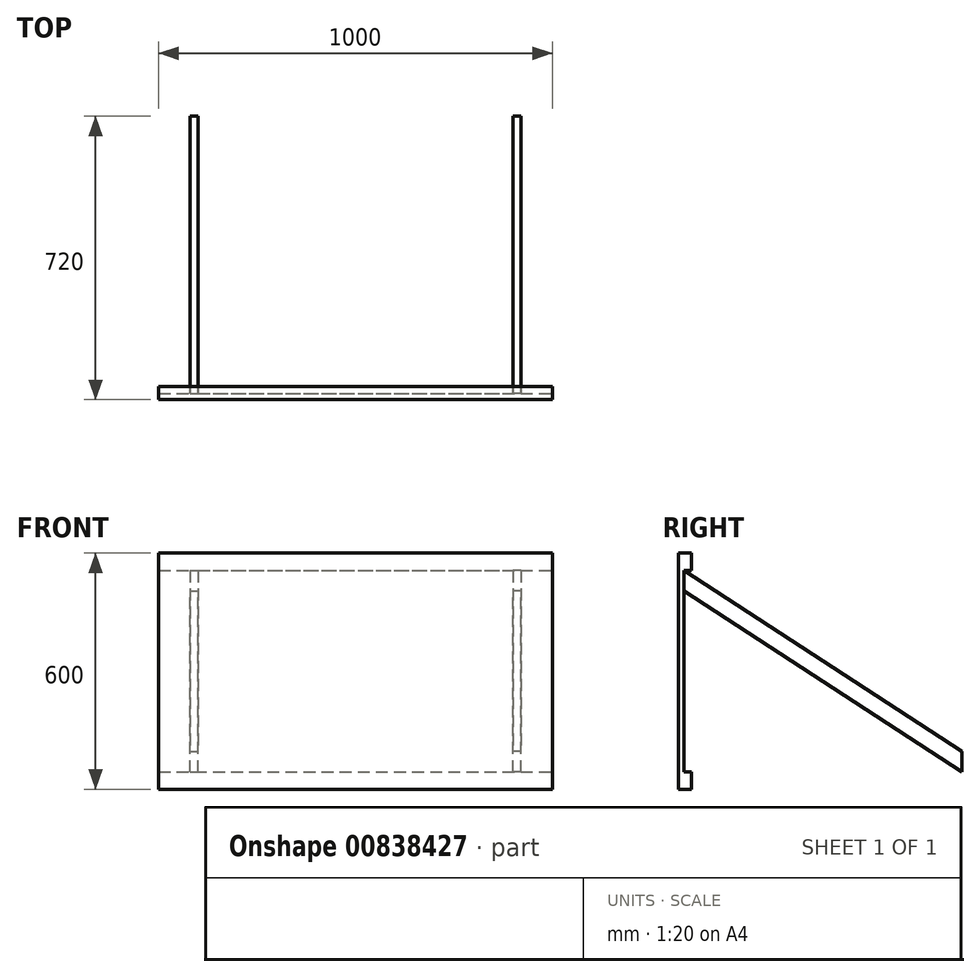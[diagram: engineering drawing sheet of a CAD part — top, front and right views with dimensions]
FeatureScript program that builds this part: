
annotation { "Feature Type Name" : "Feature", "Feature Type Description" : "" }
export const myFeature = defineFeature(function(context is Context, id is Id, definition is map)
    precondition{}
    {
        {
            var Q0;
            Q0=qCreatedBy(makeId("Front.planeOp"),FACE);
            var sketch = newSketch(context, id + "F0", { "sketchPlane" : qUnion([Q0])});
            skLineSegment(sketch, "E0.bottom", {"start": v(500, 0) * mm, "end": v(-500, 0) * mm});
            skLineSegment(sketch, "E0.top", {"start": v(500, 600) * mm, "end": v(-500, 600) * mm});
            skLineSegment(sketch, "E0.left", {"start": v(500, 0) * mm, "end": v(500, 600) * mm});
            skLineSegment(sketch, "E0.right", {"start": v(-500, 0) * mm, "end": v(-500, 600) * mm});
            skSolve(sketch);
        }
        {
            var Q0;
            Q0 = qSketchRegion(id + "F0", true);
            extrude(context, id + "F1", {"entities" : qUnion([Q0]), "depth" : 15 * mm, "offsetDistance" : 25 * mm});
        }
        {
            var Q0;
            Q0=makeQuery(id+"F1.opExtrude","CAP_FACE",FACE,{"disambiguationData":[OSD([sQuery(id+"F0.wireOp",EDGE,"E0.bottom"),sQuery(id+"F0.wireOp",EDGE,"E0.top"),sQuery(id+"F0.wireOp",EDGE,"E0.left"),sQuery(id+"F0.wireOp",EDGE,"E0.right")])],"isStart":true});
            cPlane(context, id + "F2", {"entities" : qUnion([Q0]), "cplaneType" : CPlaneType.OFFSET, "offset" : 0 * mm, "width" : 150 * mm, "height" : 150 * mm});
        }
        {
            var Q0;
            Q0=qCreatedBy(id+"F2.planeOp",FACE);
            var sketch = newSketch(context, id + "F3", { "sketchPlane" : qUnion([Q0])});
            skLineSegment(sketch, "E1.bottom", {"start": v(500, 0) * mm, "end": v(-500, 0) * mm});
            skLineSegment(sketch, "E1.top", {"start": v(500, 44) * mm, "end": v(-500, 44) * mm});
            skLineSegment(sketch, "E1.left", {"start": v(500, 0) * mm, "end": v(500, 44) * mm});
            skLineSegment(sketch, "E1.right", {"start": v(-500, 0) * mm, "end": v(-500, 44) * mm});
            skSolve(sketch);
        }
        {
            var Q0;
            Q0 = qSketchRegion(id + "F3", true);
            extrude(context, id + "F4", {"entities" : qUnion([Q0]), "operationType" : NewBodyOperationType.ADD, "depth" : 18 * mm, "offsetDistance" : 25 * mm});
        }
        {
            var Q0;
            Q0=qCreatedBy(id+"F2.planeOp",FACE);
            var sketch = newSketch(context, id + "F5", { "sketchPlane" : qUnion([Q0])});
            skLineSegment(sketch, "E2.bottom", {"start": v(500, 600) * mm, "end": v(-500, 600) * mm});
            skLineSegment(sketch, "E2.top", {"start": v(500, 556) * mm, "end": v(-500, 556) * mm});
            skLineSegment(sketch, "E2.left", {"start": v(500, 600) * mm, "end": v(500, 556) * mm});
            skLineSegment(sketch, "E2.right", {"start": v(-500, 600) * mm, "end": v(-500, 556) * mm});
            skSolve(sketch);
        }
        {
            var Q0;
            Q0 = qSketchRegion(id + "F5", true);
            extrude(context, id + "F6", {"entities" : qUnion([Q0]), "operationType" : NewBodyOperationType.ADD, "depth" : 18 * mm, "offsetDistance" : 25 * mm});
        }
        {
            var Q0;
            Q0=makeQuery(id+"F6.boolean.opBoolean","MERGE",FACE,{"derivedFrom":[makeQuery(id+"F4.boolean.opBoolean","MERGE",FACE,{"derivedFrom":[makeQuery(id+"F1.opExtrude","SWEPT_FACE",FACE,{"disambiguationData":[OSD([sQuery(id+"F0.wireOp",EDGE,"E0.right")])]}),makeQuery(id+"F4.opExtrude","SWEPT_FACE",FACE,{"disambiguationData":[OSD([sQuery(id+"F3.wireOp",EDGE,"E1.left")])]})]}),makeQuery(id+"F6.opExtrude","SWEPT_FACE",FACE,{"disambiguationData":[OSD([sQuery(id+"F5.wireOp",EDGE,"E2.left")])]})]});
            cPlane(context, id + "F7", {"entities" : qUnion([Q0]), "cplaneType" : CPlaneType.OFFSET, "offset" : 100 * mm, "oppositeDirection" : true, "width" : 150 * mm, "height" : 150 * mm});
        }
        {
            var Q0;
            Q0=qCreatedBy(id+"F7.planeOp",FACE);
            var sketch = newSketch(context, id + "F8", { "sketchPlane" : qUnion([Q0])});
            skLineSegment(sketch, "E3", {"start": v(0, 556) * mm, "end": v(-705, 96.52) * mm});
            skLineSegment(sketch, "E4", {"start": v(0, 600) * mm, "end": v(0, 556) * mm, "construction": true});
            skLineSegment(sketch, "E5", {"start": v(0, 600) * mm, "end": v(-18, 600) * mm, "construction": true});
            skLineSegment(sketch, "E6", {"start": v(0, 91.51) * mm, "end": v(-17.92, 91.51) * mm, "construction": true});
            skLineSegment(sketch, "E7", {"start": v(0, 44) * mm, "end": v(-705, 44) * mm, "construction": true});
            skLineSegment(sketch, "E8", {"start": v(-705, 44) * mm, "end": v(0, 503.48) * mm});
            skLineSegment(sketch, "E9", {"start": v(0, 556) * mm, "end": v(0, 503.48) * mm});
            skLineSegment(sketch, "E10", {"start": v(-705, 44) * mm, "end": v(-705, 96.52) * mm});
            skSolve(sketch);
        }
        {
            var Q0;
            Q0=makeQuery(id+"F8.imprint","IMPRINT",FACE,{"disambiguationData":[TD([[makeQuery(id+"F8.imprint","IMPRINT",EDGE,{"derivedFrom":sQuery(id+"F8.wireOp",EDGE,"E3")}),1.0]])]});
            extrude(context, id + "F9", {"entities" : qUnion([Q0]), "operationType" : NewBodyOperationType.ADD, "depth" : 20 * mm, "offsetDistance" : 25 * mm});
        }
        {
            var Q0;
            Q0=makeQuery(id+"F1.opExtrude","SWEPT_BODY",BODY,{"disambiguationData":[OSD([sQuery(id+"F0.wireOp",EDGE,"E0.bottom"),sQuery(id+"F0.wireOp",EDGE,"E0.top"),sQuery(id+"F0.wireOp",EDGE,"E0.left"),sQuery(id+"F0.wireOp",EDGE,"E0.right")])]});
            var Q1;
            Q1=qCreatedBy(makeId("Right.planeOp"),FACE);
            mirror(context, id + "F10", {"operationType" : NewBodyOperationType.ADD, "entities" : qUnion([Q0]), "mirrorPlane" : qUnion([Q1])});
        }
        {
            var Q0;
            Q0=makeQuery(id+"F9.opExtrude","CAP_FACE",FACE,{"disambiguationData":[OSD([sQuery(id+"F8.wireOp",EDGE,"E3"),sQuery(id+"F8.wireOp",EDGE,"E8"),sQuery(id+"F8.wireOp",EDGE,"E9"),sQuery(id+"F8.wireOp",EDGE,"E10")])],"isStart":false});
            cPlane(context, id + "F11", {"entities" : qUnion([Q0]), "cplaneType" : CPlaneType.OFFSET, "offset" : 0 * mm, "width" : 150 * mm, "height" : 150 * mm});
        }
    });
